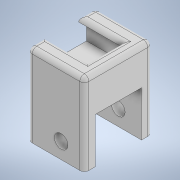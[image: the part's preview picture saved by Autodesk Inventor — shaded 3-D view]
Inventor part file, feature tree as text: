
AUTODESK INVENTOR PART (.ipt)
format: ipt  version: 2021.4 (Build 254397000, 397)  size: 196,096 bytes
history: native  units: mm
features: sketch x9, extrude x7, other x1, hole x1, fillet x1
ambient origin geometry x8: Origin, YZ Plane, XZ Plane, XY Plane, X Axis, Y Axis, Z Axis, Center Point
bodies: Body1 (feature_tree)
feature tree (19):
  other  "ソリッド1"
  extrude  "押し出し1"  Depth=25.0mm
  extrude  "押し出し2"  Depth=30.0mm
  hole  "穴1"  [1 undecoded]
  extrude  "押し出し4"  Depth=20.5mm
  extrude  "押し出し5"  Depth=20.5mm
  sketch  "スケッチ8"
  extrude  "押し出し7"  Depth=20.0mm TaperAngle=0.0deg
  extrude  "押し出し8"  Depth=7.0mm
  extrude  "押し出し9"  Depth=10.25mm
  fillet  "フィレット3"  Radius=10.25mm
  sketch  "スケッチ1"
  sketch  "スケッチ2"
  sketch  "スケッチ4"
  sketch  "スケッチ5"
  sketch  "スケッチ6"
  sketch  "スケッチ9"
  sketch  "スケッチ10"
  sketch  "スケッチ12"
note: 1 required parameter value undecoded (feature->parameter linkage not recoverable at this tier; creation-order binding heuristic only, values carry confidence <= 0.55)
